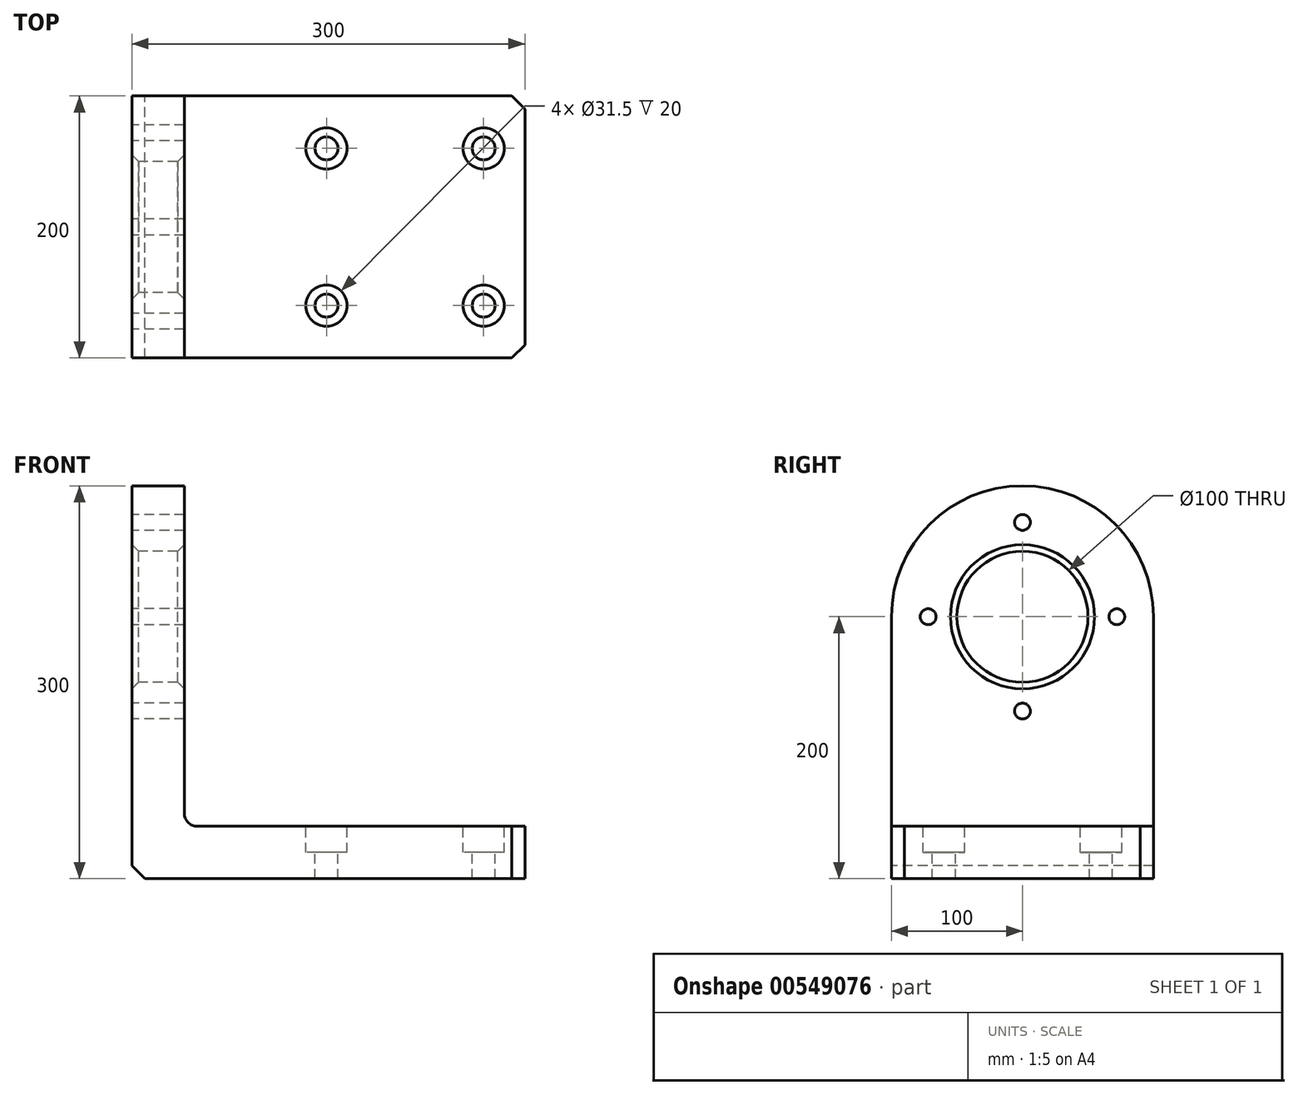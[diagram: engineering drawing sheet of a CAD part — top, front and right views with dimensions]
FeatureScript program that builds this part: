
annotation { "Feature Type Name" : "Feature", "Feature Type Description" : "" }
export const myFeature = defineFeature(function(context is Context, id is Id, definition is map)
    precondition{}
    {
        {
            var Q0;
            Q0=qCreatedBy(makeId("Front.planeOp"),FACE);
            var sketch = newSketch(context, id + "F0", { "sketchPlane" : qUnion([Q0])});
            skLineSegment(sketch, "E0.bottom", {"start": v(0, 0) * mm, "end": v(290, 0) * mm});
            skLineSegment(sketch, "E0.top", {"start": v(0, 40) * mm, "end": v(290, 40) * mm});
            skLineSegment(sketch, "E0.left", {"start": v(0, 0) * mm, "end": v(0, 40) * mm});
            skLineSegment(sketch, "E1", {"start": v(290, 40) * mm, "end": v(290, 0) * mm});
            skLineSegment(sketch, "E2.bottom", {"start": v(0, 0) * mm, "end": v(40, 0) * mm});
            skLineSegment(sketch, "E2.left", {"start": v(0, 0) * mm, "end": v(0, 200) * mm});
            skLineSegment(sketch, "E2.right", {"start": v(40, 0) * mm, "end": v(40, 200) * mm});
            skLineSegment(sketch, "E3", {"start": v(0, 200) * mm, "end": v(40, 200) * mm});
            skPoint(sketch, "E4.orphan", {"position": v(300, 40) * mm});
            skSolve(sketch);
        }
        {
            var Q0;
            Q0=qCreatedBy(makeId("Right.planeOp"),FACE);
            var sketch = newSketch(context, id + "F1", { "sketchPlane" : qUnion([Q0])});
            skLineSegment(sketch, "E5.bottom", {"start": v(0, 0) * mm, "end": v(200, 0) * mm});
            skLineSegment(sketch, "E5.top", {"start": v(0, 40) * mm, "end": v(200, 40) * mm});
            skLineSegment(sketch, "E5.left", {"start": v(0, 0) * mm, "end": v(0, 40) * mm});
            skLineSegment(sketch, "E5.right", {"start": v(200, 0) * mm, "end": v(200, 40) * mm});
            skLineSegment(sketch, "E6", {"start": v(10, 40) * mm, "end": v(10, 0) * mm});
            skLineSegment(sketch, "E7", {"start": v(190, 40) * mm, "end": v(190, 0) * mm});
            skLineSegment(sketch, "E8.top", {"start": v(0, 200) * mm, "end": v(200, 200) * mm});
            skLineSegment(sketch, "E8.left", {"start": v(0, 0) * mm, "end": v(0, 200) * mm});
            skLineSegment(sketch, "E8.right", {"start": v(200, 0) * mm, "end": v(200, 200) * mm});
            skCircle(sketch, "E9", {"center": v(100, 200) * mm, "radius": 100 * mm});
            skCircle(sketch, "E10", {"center": v(100, 200) * mm, "radius": 50 * mm});
            skPoint(sketch, "E11", {"position": v(100, 272) * mm});
            skPoint(sketch, "E12.1.0", {"position": v(28, 200) * mm});
            skPoint(sketch, "E12.2.0", {"position": v(100, 128) * mm});
            skPoint(sketch, "E13.0.3.0", {"position": v(172, 200) * mm});
            skSolve(sketch);
        }
        {
            var Q0;
            Q0 = qSketchRegion(id + "F1", true);
            extrude(context, id + "F2", {"entities" : qUnion([Q0]), "depth" : 40 * mm, "offsetDistance" : 25 * mm});
        }
        {
            var Q0;
            Q0=sQuery(id+"F1.wireOp",VERTEX,"E11");
            var Q1;
            Q1=sQuery(id+"F1.wireOp",VERTEX,"E12.2.0");
            var Q2;
            Q2=sQuery(id+"F1.wireOp",VERTEX,"E13.0.3.0");
            var Q3;
            Q3=sQuery(id+"F1.wireOp",VERTEX,"E12.1.0");
            var Q4;
            Q4=makeQuery(id+"F2.opExtrude","SWEPT_BODY",BODY,{"disambiguationData":[OSD([sQuery(id+"F1.wireOp",EDGE,"E5.bottom"),sQuery(id+"F1.wireOp",EDGE,"E8.left"),sQuery(id+"F1.wireOp",EDGE,"E8.right"),sQuery(id+"F1.wireOp",EDGE,"E9"),sQuery(id+"F1.wireOp",EDGE,"E10")])]});
            hole(context, id + "F3", {"style" : HoleStyle.SIMPLE, "endStyle" : HoleEndStyle.THROUGH, "oppositeDirection" : true, "standardTappedOrClearance" : lookupTablePath({ "standard" : "ISO", "engagement" : "75%", "pitch" : "2 mm", "size" : "M14", "type" : "Tapped" }), "standardBlindInLast" : lookupTablePath({ "standard" : "ISO", "engagement" : "75%", "pitch" : "2 mm", "size" : "M14", "type" : "Tapped" }), "holeDiameter" : 12.1 * mm, "showTappedDepth" : true, "isTappedThrough" : true, "tappedDepth" : 12 * mm, "tapClearance" : 3, "locations" : qUnion([Q0, Q1, Q2, Q3]), "scope" : qUnion([Q4]), "majorDiameter" : 14 * mm});
        }
        {
            var Q0;
            Q0=qCreatedBy(makeId("Top.planeOp"),FACE);
            var sketch = newSketch(context, id + "F4", { "sketchPlane" : qUnion([Q0])});
            skLineSegment(sketch, "E14.bottom", {"start": v(0, 0) * mm, "end": v(300, 0) * mm});
            skLineSegment(sketch, "E14.top", {"start": v(0, 200) * mm, "end": v(300, 200) * mm});
            skLineSegment(sketch, "E14.left", {"start": v(0, 0) * mm, "end": v(0, 200) * mm});
            skLineSegment(sketch, "E14.right", {"start": v(300, 0) * mm, "end": v(300, 200) * mm});
            skSolve(sketch);
        }
        {
            var Q0;
            Q0 = qSketchRegion(id + "F4", true);
            extrude(context, id + "F5", {"entities" : qUnion([Q0]), "operationType" : NewBodyOperationType.ADD, "depth" : 40 * mm, "offsetDistance" : 25 * mm});
        }
        {
            var Q0;
            Q0=makeQuery(id+"F5.opExtrude","SWEPT_EDGE",EDGE,{"disambiguationData":[OSD([sQuery(id+"F4.wireOp",EDGE,"E14.bottom"),sQuery(id+"F4.wireOp",EDGE,"E14.right")])]});
            chamfer(context, id + "F6", {"entities" : qUnion([Q0]), "width" : 10 * mm, "tangentPropagation" : true});
        }
        {
            var Q0;
            Q0=makeQuery(id+"F5.opExtrude","SWEPT_EDGE",EDGE,{"disambiguationData":[OSD([sQuery(id+"F4.wireOp",EDGE,"E14.top"),sQuery(id+"F4.wireOp",EDGE,"E14.right")])]});
            chamfer(context, id + "F7", {"entities" : qUnion([Q0]), "width" : 10 * mm, "tangentPropagation" : true});
        }
        {
            var Q0;
            Q0=makeQuery(id+"F2.opExtrude","CAP_EDGE",EDGE,{"disambiguationData":[OSD([sQuery(id+"F1.wireOp",EDGE,"E5.bottom")])],"isStart":true});
            chamfer(context, id + "F8", {"entities" : qUnion([Q0]), "width" : 10 * mm, "tangentPropagation" : true});
        }
        {
            var Q0;
            Q0=makeQuery(id+"F5.boolean.opBoolean","INTERSECT",EDGE,{"derivedFrom":[makeQuery(id+"F2.opExtrude","CAP_FACE",FACE,{"disambiguationData":[OSD([sQuery(id+"F1.wireOp",EDGE,"E5.bottom"),sQuery(id+"F1.wireOp",EDGE,"E8.left"),sQuery(id+"F1.wireOp",EDGE,"E8.right"),sQuery(id+"F1.wireOp",EDGE,"E9"),sQuery(id+"F1.wireOp",EDGE,"E10")])],"isStart":false}),makeQuery(id+"F5.opExtrude","CAP_FACE",FACE,{"disambiguationData":[OSD([sQuery(id+"F4.wireOp",EDGE,"E14.bottom"),sQuery(id+"F4.wireOp",EDGE,"E14.top"),sQuery(id+"F4.wireOp",EDGE,"E14.left"),sQuery(id+"F4.wireOp",EDGE,"E14.right")])],"isStart":false})]});
            fillet(context, id + "F9", {"entities" : qUnion([Q0]), "radius" : 10 * mm, "tangentPropagation" : true, "allowEdgeOverflow" : false});
        }
        {
            var Q0;
            Q0=makeQuery(id+"F2.opExtrude","CAP_EDGE",EDGE,{"disambiguationData":[OSD([sQuery(id+"F1.wireOp",EDGE,"E10")])],"isStart":false});
            var Q1;
            Q1=makeQuery(id+"F2.opExtrude","CAP_EDGE",EDGE,{"disambiguationData":[OSD([sQuery(id+"F1.wireOp",EDGE,"E10")])],"isStart":true});
            chamfer(context, id + "F10", {"entities" : qUnion([Q0, Q1]), "width" : 5 * mm, "tangentPropagation" : true});
        }
        {
            var Q0;
            Q0=makeQuery(id+"F5.opExtrude","CAP_FACE",FACE,{"disambiguationData":[OSD([sQuery(id+"F4.wireOp",EDGE,"E14.bottom"),sQuery(id+"F4.wireOp",EDGE,"E14.top"),sQuery(id+"F4.wireOp",EDGE,"E14.left"),sQuery(id+"F4.wireOp",EDGE,"E14.right")])],"isStart":false});
            var sketch = newSketch(context, id + "F11", { "sketchPlane" : qUnion([Q0])});
            skCircle(sketch, "E15", {"center": v(268.5, 40) * mm, "radius": 17 * mm});
            skCircle(sketch, "E16.0.1.0", {"center": v(268.5, 160) * mm, "radius": 17 * mm});
            skCircle(sketch, "E16.1.0.0", {"center": v(148.5, 40) * mm, "radius": 17 * mm});
            skCircle(sketch, "E16.1.1.0", {"center": v(148.5, 160) * mm, "radius": 17 * mm});
            skLineSegment(sketch, "E16.direction1", {"start": v(260, 40) * mm, "end": v(140, 40) * mm, "construction": true});
            skLineSegment(sketch, "E16.direction2", {"start": v(260, 40) * mm, "end": v(260, 160) * mm, "construction": true});
            skSolve(sketch);
        }
        {
            var Q0;
            Q0=sQuery(id+"F11.wireOp",VERTEX,"E15.center");
            var Q1;
            Q1=sQuery(id+"F11.wireOp",VERTEX,"E16.1.0.0.center");
            var Q2;
            Q2=sQuery(id+"F11.wireOp",VERTEX,"E16.1.1.0.center");
            var Q3;
            Q3=sQuery(id+"F11.wireOp",VERTEX,"E16.0.1.0.center");
            var Q4;
            Q4=makeQuery(id+"F2.opExtrude","SWEPT_BODY",BODY,{"disambiguationData":[OSD([sQuery(id+"F1.wireOp",EDGE,"E5.bottom"),sQuery(id+"F1.wireOp",EDGE,"E8.left"),sQuery(id+"F1.wireOp",EDGE,"E8.right"),sQuery(id+"F1.wireOp",EDGE,"E9"),sQuery(id+"F1.wireOp",EDGE,"E10")])]});
            hole(context, id + "F12", {"style" : HoleStyle.C_BORE, "endStyle" : HoleEndStyle.THROUGH, "holeDiameter" : 17.5 * mm, "cBoreDiameter" : 31.5 * mm, "cBoreDepth" : 20 * mm, "isTappedThrough" : true, "tappedDepth" : 12 * mm, "tapClearance" : 3, "locations" : qUnion([Q0, Q1, Q2, Q3]), "scope" : qUnion([Q4])});
        }
    });
